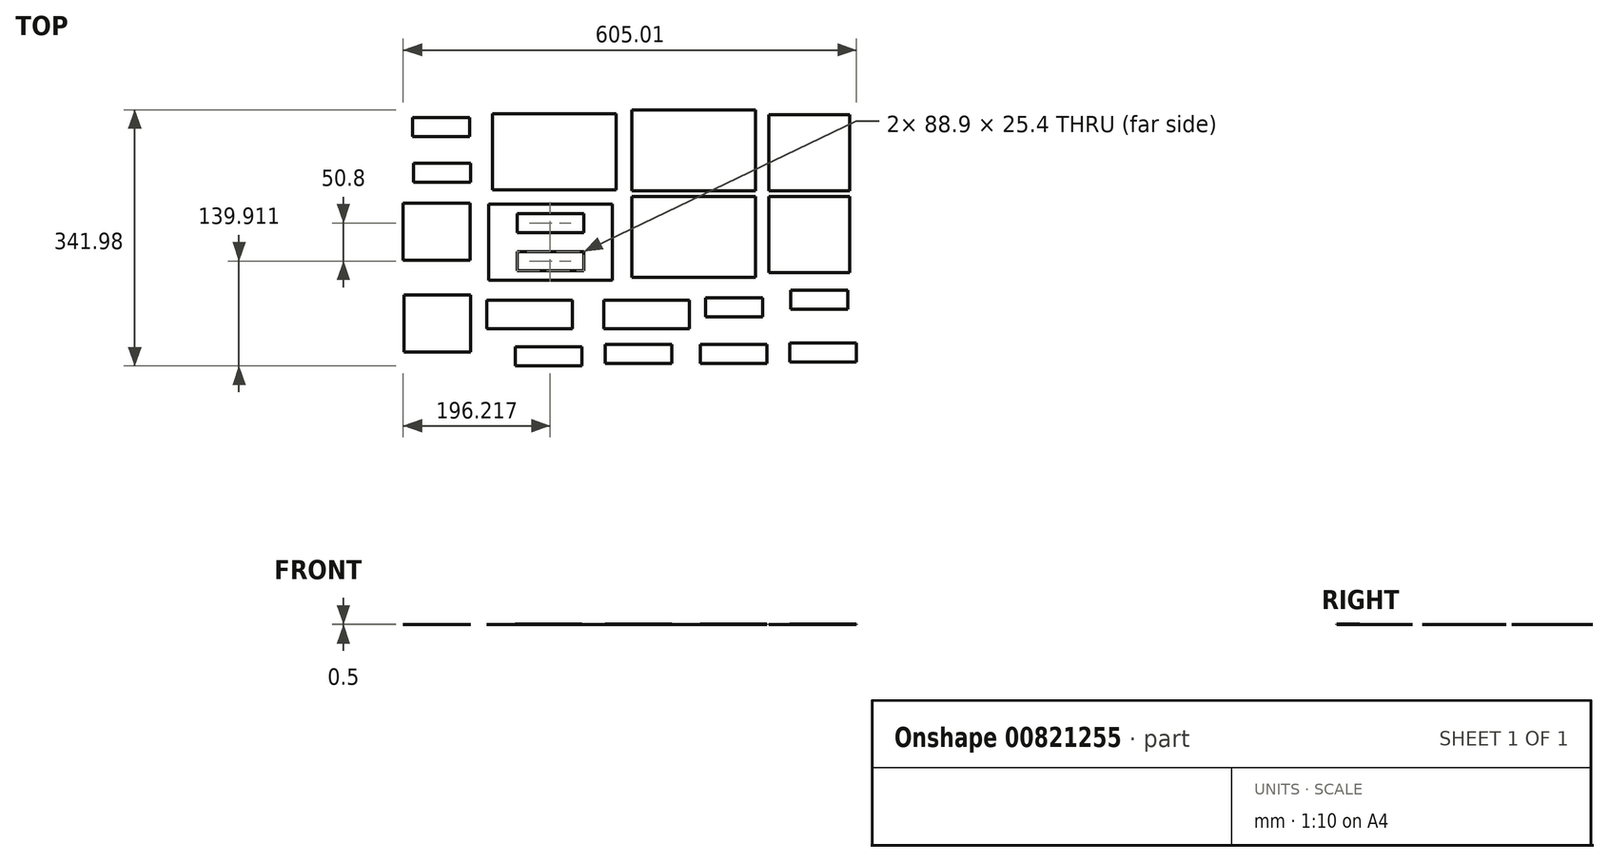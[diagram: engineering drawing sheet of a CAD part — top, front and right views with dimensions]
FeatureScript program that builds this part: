
annotation { "Feature Type Name" : "Feature", "Feature Type Description" : "" }
export const myFeature = defineFeature(function(context is Context, id is Id, definition is map)
    precondition{}
    {
        {
            assignVariable(context, id + "F0", {"name" : "th", "anyValue" : .25});
        }
        {
            var Q0;
            Q0=qCreatedBy(makeId("Top.planeOp"),FACE);
            var sketch = newSketch(context, id + "F1", { "sketchPlane" : qUnion([Q0])});
            skLineSegment(sketch, "E0.bottom", {"start": v(-137.52, 115.81) * mm, "end": v(27.58, 115.81) * mm});
            skLineSegment(sketch, "E0.top", {"start": v(-137.52, 7.86) * mm, "end": v(27.58, 7.86) * mm});
            skLineSegment(sketch, "E0.left", {"start": v(-137.52, 115.81) * mm, "end": v(-137.52, 7.86) * mm});
            skLineSegment(sketch, "E0.right", {"start": v(27.58, 115.81) * mm, "end": v(27.58, 7.86) * mm});
            skSolve(sketch);
        }
        {
            var Q0;
            Q0=qCreatedBy(makeId("Top.planeOp"),FACE);
            var sketch = newSketch(context, id + "F2", { "sketchPlane" : qUnion([Q0])});
            skLineSegment(sketch, "E1.bottom", {"start": v(-137.34, 0) * mm, "end": v(27.76, 0) * mm});
            skLineSegment(sketch, "E1.top", {"start": v(-137.34, -107.95) * mm, "end": v(27.76, -107.95) * mm});
            skLineSegment(sketch, "E1.left", {"start": v(-137.34, 0) * mm, "end": v(-137.34, -107.95) * mm});
            skLineSegment(sketch, "E1.right", {"start": v(27.76, 0) * mm, "end": v(27.76, -107.95) * mm});
            skSolve(sketch);
        }
        {
            var Q0;
            Q0=qCreatedBy(makeId("Top.planeOp"),FACE);
            var sketch = newSketch(context, id + "F3", { "sketchPlane" : qUnion([Q0])});
            skLineSegment(sketch, "E2.bottom", {"start": v(45.43, 109.05) * mm, "end": v(153.38, 109.05) * mm});
            skLineSegment(sketch, "E2.top", {"start": v(45.43, 7.45) * mm, "end": v(153.38, 7.45) * mm});
            skLineSegment(sketch, "E2.left", {"start": v(45.43, 109.05) * mm, "end": v(45.43, 7.45) * mm});
            skLineSegment(sketch, "E2.right", {"start": v(153.38, 109.05) * mm, "end": v(153.38, 7.45) * mm});
            skSolve(sketch);
        }
        {
            var Q0;
            Q0=qCreatedBy(makeId("Top.planeOp"),FACE);
            var sketch = newSketch(context, id + "F4", { "sketchPlane" : qUnion([Q0])});
            skLineSegment(sketch, "E3.bottom", {"start": v(45.42, 0) * mm, "end": v(153.37, 0) * mm});
            skLineSegment(sketch, "E3.top", {"start": v(45.42, -101.6) * mm, "end": v(153.37, -101.6) * mm});
            skLineSegment(sketch, "E3.left", {"start": v(45.42, 0) * mm, "end": v(45.42, -101.6) * mm});
            skLineSegment(sketch, "E3.right", {"start": v(153.37, 0) * mm, "end": v(153.37, -101.6) * mm});
            skSolve(sketch);
        }
        {
            var Q0;
            Q0=qCreatedBy(makeId("Top.planeOp"),FACE);
            var sketch = newSketch(context, id + "F5", { "sketchPlane" : qUnion([Q0])});
            skLineSegment(sketch, "E4.bottom", {"start": v(-163.54, -111.66) * mm, "end": v(-328.64, -111.66) * mm});
            skLineSegment(sketch, "E4.top", {"start": v(-163.54, -10.06) * mm, "end": v(-328.64, -10.06) * mm});
            skLineSegment(sketch, "E4.left", {"start": v(-163.54, -111.66) * mm, "end": v(-163.54, -10.06) * mm});
            skLineSegment(sketch, "E4.right", {"start": v(-328.64, -111.66) * mm, "end": v(-328.64, -10.06) * mm});
            skSolve(sketch);
        }
        {
            var Q0;
            Q0=qCreatedBy(makeId("Top.planeOp"),FACE);
            var sketch = newSketch(context, id + "F6", { "sketchPlane" : qUnion([Q0])});
            skLineSegment(sketch, "E5.bottom", {"start": v(-323.3, 9.04) * mm, "end": v(-158.2, 9.04) * mm});
            skLineSegment(sketch, "E5.top", {"start": v(-323.3, 110.64) * mm, "end": v(-158.2, 110.64) * mm});
            skLineSegment(sketch, "E5.left", {"start": v(-323.3, 9.04) * mm, "end": v(-323.3, 110.64) * mm});
            skLineSegment(sketch, "E5.right", {"start": v(-158.2, 9.04) * mm, "end": v(-158.2, 110.64) * mm});
            skSolve(sketch);
        }
        {
            var Q0;
            Q0=makeQuery(id+"F1.imprint","IMPRINT",FACE,{"disambiguationData":[TD([[makeQuery(id+"F1.imprint","IMPRINT",EDGE,{"derivedFrom":sQuery(id+"F1.wireOp",EDGE,"E0.bottom")}),-1.0]])]});
            var Q1;
            Q1=makeQuery(id+"F2.imprint","IMPRINT",FACE,{"disambiguationData":[TD([[makeQuery(id+"F2.imprint","IMPRINT",EDGE,{"derivedFrom":sQuery(id+"F2.wireOp",EDGE,"E1.bottom")}),-1.0]])]});
            var Q2;
            Q2=makeQuery(id+"F3.imprint","IMPRINT",FACE,{"disambiguationData":[TD([[makeQuery(id+"F3.imprint","IMPRINT",EDGE,{"derivedFrom":sQuery(id+"F3.wireOp",EDGE,"E2.bottom")}),-1.0]])]});
            var Q3;
            Q3=makeQuery(id+"F4.imprint","IMPRINT",FACE,{"disambiguationData":[TD([[makeQuery(id+"F4.imprint","IMPRINT",EDGE,{"derivedFrom":sQuery(id+"F4.wireOp",EDGE,"E3.bottom")}),-1.0]])]});
            var Q4;
            Q4=makeQuery(id+"F5.imprint","IMPRINT",FACE,{"disambiguationData":[TD([[makeQuery(id+"F5.imprint","IMPRINT",EDGE,{"derivedFrom":sQuery(id+"F5.wireOp",EDGE,"E4.bottom")}),-1.0]])]});
            var Q5;
            Q5=qSketchRegion(id+"F6",true);
            extrude(context, id + "F7", {"entities" : qUnion([Q0, Q1, Q2, Q3, Q4, Q5]), "depth" : (getVariable(context, 'th')) * mm, "offsetDistance" : 25.4 * mm});
        }
        {
            var Q0;
            Q0=makeQuery(id+"F7.opExtrude","CAP_FACE",FACE,{"disambiguationData":[OSD([sQuery(id+"F5.wireOp",EDGE,"E4.bottom"),sQuery(id+"F5.wireOp",EDGE,"E4.top"),sQuery(id+"F5.wireOp",EDGE,"E4.left"),sQuery(id+"F5.wireOp",EDGE,"E4.right")])],"isStart":false});
            var sketch = newSketch(context, id + "F8", { "sketchPlane" : qUnion([Q0])});
            skLineSegment(sketch, "E6.bottom", {"start": v(-290.54, -98.96) * mm, "end": v(-201.64, -98.96) * mm});
            skLineSegment(sketch, "E6.top", {"start": v(-290.54, -73.56) * mm, "end": v(-201.64, -73.56) * mm});
            skLineSegment(sketch, "E6.left", {"start": v(-290.54, -98.96) * mm, "end": v(-290.54, -73.56) * mm});
            skLineSegment(sketch, "E6.right", {"start": v(-201.64, -98.96) * mm, "end": v(-201.64, -73.56) * mm});
            skLineSegment(sketch, "E7.bottom", {"start": v(-303.24, -105.3) * mm, "end": v(-188.94, -105.3) * mm, "construction": true});
            skLineSegment(sketch, "E7.top", {"start": v(-303.24, -67.2) * mm, "end": v(-188.94, -67.2) * mm, "construction": true});
            skLineSegment(sketch, "E7.left", {"start": v(-303.24, -105.3) * mm, "end": v(-303.24, -67.2) * mm, "construction": true});
            skLineSegment(sketch, "E7.right", {"start": v(-188.94, -105.3) * mm, "end": v(-188.94, -67.2) * mm, "construction": true});
            skLineSegment(sketch, "E8.bottom", {"start": v(-290.54, -48.16) * mm, "end": v(-201.64, -48.16) * mm});
            skLineSegment(sketch, "E8.top", {"start": v(-290.54, -22.76) * mm, "end": v(-201.64, -22.76) * mm});
            skLineSegment(sketch, "E8.left", {"start": v(-290.54, -48.16) * mm, "end": v(-290.54, -22.76) * mm});
            skLineSegment(sketch, "E8.right", {"start": v(-201.64, -48.16) * mm, "end": v(-201.64, -22.76) * mm});
            skLineSegment(sketch, "E9.bottom", {"start": v(-303.24, -54.5) * mm, "end": v(-188.94, -54.5) * mm, "construction": true});
            skLineSegment(sketch, "E9.top", {"start": v(-303.24, -16.4) * mm, "end": v(-188.94, -16.4) * mm, "construction": true});
            skLineSegment(sketch, "E9.left", {"start": v(-303.24, -54.5) * mm, "end": v(-303.24, -16.4) * mm, "construction": true});
            skLineSegment(sketch, "E9.right", {"start": v(-188.94, -54.5) * mm, "end": v(-188.94, -16.4) * mm, "construction": true});
            skLineSegment(sketch, "E10", {"start": v(-328.64, -60.86) * mm, "end": v(-163.54, -60.86) * mm, "construction": true});
            skSolve(sketch);
        }
        {
            var Q0;
            Q0=qSketchRegion(id+"F8",true);
            extrude(context, id + "F9", {"entities" : qUnion([Q0]), "operationType" : NewBodyOperationType.REMOVE, "endBound" : BoundingType.THROUGH_ALL, "oppositeDirection" : true, "depth" : 25.4 * mm, "offsetDistance" : 25.4 * mm});
        }
        {
            var Q0;
            Q0=qCreatedBy(makeId("Top.planeOp"),FACE);
            var sketch = newSketch(context, id + "F10", { "sketchPlane" : qUnion([Q0])});
            skLineSegment(sketch, "E11.bottom", {"start": v(-174.86, -176.3) * mm, "end": v(-60.56, -176.3) * mm});
            skLineSegment(sketch, "E11.top", {"start": v(-174.86, -138.2) * mm, "end": v(-60.56, -138.2) * mm});
            skLineSegment(sketch, "E11.left", {"start": v(-174.86, -176.3) * mm, "end": v(-174.86, -138.2) * mm});
            skLineSegment(sketch, "E11.right", {"start": v(-60.56, -176.3) * mm, "end": v(-60.56, -138.2) * mm});
            skLineSegment(sketch, "E12.bottom", {"start": v(-330.87, -176.3) * mm, "end": v(-216.57, -176.3) * mm});
            skLineSegment(sketch, "E12.top", {"start": v(-330.87, -138.2) * mm, "end": v(-216.57, -138.2) * mm});
            skLineSegment(sketch, "E12.left", {"start": v(-330.87, -176.3) * mm, "end": v(-330.87, -138.2) * mm});
            skLineSegment(sketch, "E12.right", {"start": v(-216.57, -176.3) * mm, "end": v(-216.57, -138.2) * mm});
            skSolve(sketch);
        }
        {
            var Q0;
            Q0=qCreatedBy(makeId("Top.planeOp"),FACE);
            var sketch = newSketch(context, id + "F11", { "sketchPlane" : qUnion([Q0])});
            skLineSegment(sketch, "E13.bottom", {"start": v(-38.9, -160.7) * mm, "end": v(37.3, -160.7) * mm});
            skLineSegment(sketch, "E13.top", {"start": v(-38.9, -135.3) * mm, "end": v(37.3, -135.3) * mm});
            skLineSegment(sketch, "E13.left", {"start": v(-38.9, -160.7) * mm, "end": v(-38.9, -135.3) * mm});
            skLineSegment(sketch, "E13.right", {"start": v(37.3, -160.7) * mm, "end": v(37.3, -135.3) * mm});
            skLineSegment(sketch, "E14.bottom", {"start": v(74.77, -150.66) * mm, "end": v(150.97, -150.66) * mm});
            skLineSegment(sketch, "E14.top", {"start": v(74.77, -125.26) * mm, "end": v(150.97, -125.26) * mm});
            skLineSegment(sketch, "E14.left", {"start": v(74.77, -150.66) * mm, "end": v(74.77, -125.26) * mm});
            skLineSegment(sketch, "E14.right", {"start": v(150.97, -150.66) * mm, "end": v(150.97, -125.26) * mm});
            skSolve(sketch);
        }
        {
            var Q0;
            Q0=qCreatedBy(makeId("Top.planeOp"),FACE);
            var sketch = newSketch(context, id + "F12", { "sketchPlane" : qUnion([Q0])});
            skLineSegment(sketch, "E15.bottom", {"start": v(-428.94, 18.73) * mm, "end": v(-352.74, 18.73) * mm});
            skLineSegment(sketch, "E15.top", {"start": v(-428.94, 44.13) * mm, "end": v(-352.74, 44.13) * mm});
            skLineSegment(sketch, "E15.left", {"start": v(-428.94, 18.73) * mm, "end": v(-428.94, 44.13) * mm});
            skLineSegment(sketch, "E15.right", {"start": v(-352.74, 18.73) * mm, "end": v(-352.74, 44.13) * mm});
            skLineSegment(sketch, "E16.bottom", {"start": v(-430.05, 80.02) * mm, "end": v(-353.85, 80.02) * mm});
            skLineSegment(sketch, "E16.top", {"start": v(-430.05, 105.42) * mm, "end": v(-353.85, 105.42) * mm});
            skLineSegment(sketch, "E16.left", {"start": v(-430.05, 80.02) * mm, "end": v(-430.05, 105.42) * mm});
            skLineSegment(sketch, "E16.right", {"start": v(-353.85, 80.02) * mm, "end": v(-353.85, 105.42) * mm});
            skSolve(sketch);
        }
        {
            var Q0;
            Q0=qCreatedBy(makeId("Top.planeOp"),FACE);
            var sketch = newSketch(context, id + "F13", { "sketchPlane" : qUnion([Q0])});
            skLineSegment(sketch, "E17.bottom", {"start": v(-442.31, -8.71) * mm, "end": v(-353.41, -8.71) * mm});
            skLineSegment(sketch, "E17.top", {"start": v(-442.31, -84.91) * mm, "end": v(-353.41, -84.91) * mm});
            skLineSegment(sketch, "E17.left", {"start": v(-442.31, -8.71) * mm, "end": v(-442.31, -84.91) * mm});
            skLineSegment(sketch, "E17.right", {"start": v(-353.41, -8.71) * mm, "end": v(-353.41, -84.91) * mm});
            skLineSegment(sketch, "E18.bottom", {"start": v(-441.2, -131.3) * mm, "end": v(-352.3, -131.3) * mm});
            skLineSegment(sketch, "E18.top", {"start": v(-441.2, -207.5) * mm, "end": v(-352.3, -207.5) * mm});
            skLineSegment(sketch, "E18.left", {"start": v(-441.2, -131.3) * mm, "end": v(-441.2, -207.5) * mm});
            skLineSegment(sketch, "E18.right", {"start": v(-352.3, -131.3) * mm, "end": v(-352.3, -207.5) * mm});
            skSolve(sketch);
        }
        {
            var Q0;
            Q0=makeQuery(id+"F7.opExtrude","CAP_FACE",FACE,{"disambiguationData":[OSD([sQuery(id+"F2.wireOp",EDGE,"E1.bottom"),sQuery(id+"F2.wireOp",EDGE,"E1.top"),sQuery(id+"F2.wireOp",EDGE,"E1.left"),sQuery(id+"F2.wireOp",EDGE,"E1.right")])],"isStart":false});
            var sketch = newSketch(context, id + "F14", { "sketchPlane" : qUnion([Q0])});
            skLineSegment(sketch, "E19.bottom", {"start": v(-46.02, -197.7) * mm, "end": v(42.88, -197.7) * mm});
            skLineSegment(sketch, "E19.top", {"start": v(-46.02, -223.1) * mm, "end": v(42.88, -223.1) * mm});
            skLineSegment(sketch, "E19.left", {"start": v(-46.02, -197.7) * mm, "end": v(-46.02, -223.1) * mm});
            skLineSegment(sketch, "E19.right", {"start": v(42.88, -197.7) * mm, "end": v(42.88, -223.1) * mm});
            skLineSegment(sketch, "E20.bottom", {"start": v(-172.96, -197.21) * mm, "end": v(-84.06, -197.21) * mm});
            skLineSegment(sketch, "E20.top", {"start": v(-172.96, -222.61) * mm, "end": v(-84.06, -222.61) * mm});
            skLineSegment(sketch, "E20.left", {"start": v(-172.96, -197.21) * mm, "end": v(-172.96, -222.61) * mm});
            skLineSegment(sketch, "E20.right", {"start": v(-84.06, -197.21) * mm, "end": v(-84.06, -222.61) * mm});
            skLineSegment(sketch, "E21.bottom", {"start": v(-292.79, -200.77) * mm, "end": v(-203.89, -200.77) * mm});
            skLineSegment(sketch, "E21.top", {"start": v(-292.79, -226.17) * mm, "end": v(-203.89, -226.17) * mm});
            skLineSegment(sketch, "E21.left", {"start": v(-292.79, -200.77) * mm, "end": v(-292.79, -226.17) * mm});
            skLineSegment(sketch, "E21.right", {"start": v(-203.89, -200.77) * mm, "end": v(-203.89, -226.17) * mm});
            skLineSegment(sketch, "E22.bottom", {"start": v(73.8, -195.33) * mm, "end": v(162.7, -195.33) * mm});
            skLineSegment(sketch, "E22.top", {"start": v(73.8, -220.73) * mm, "end": v(162.7, -220.73) * mm});
            skLineSegment(sketch, "E22.left", {"start": v(73.8, -195.33) * mm, "end": v(73.8, -220.73) * mm});
            skLineSegment(sketch, "E22.right", {"start": v(162.7, -195.33) * mm, "end": v(162.7, -220.73) * mm});
            skSolve(sketch);
        }
        {
            var Q0;
            Q0=qSketchRegion(id+"F10",true);
            var Q1;
            Q1=qSketchRegion(id+"F11",true);
            var Q2;
            Q2=qSketchRegion(id+"F12",true);
            var Q3;
            Q3=qSketchRegion(id+"F13",true);
            var Q4;
            Q4=qSketchRegion(id+"F14",true);
            extrude(context, id + "F15", {"entities" : qUnion([Q0, Q1, Q2, Q3, Q4]), "depth" : (getVariable(context, 'th')) * mm, "offsetDistance" : 25.4 * mm});
        }
    });
